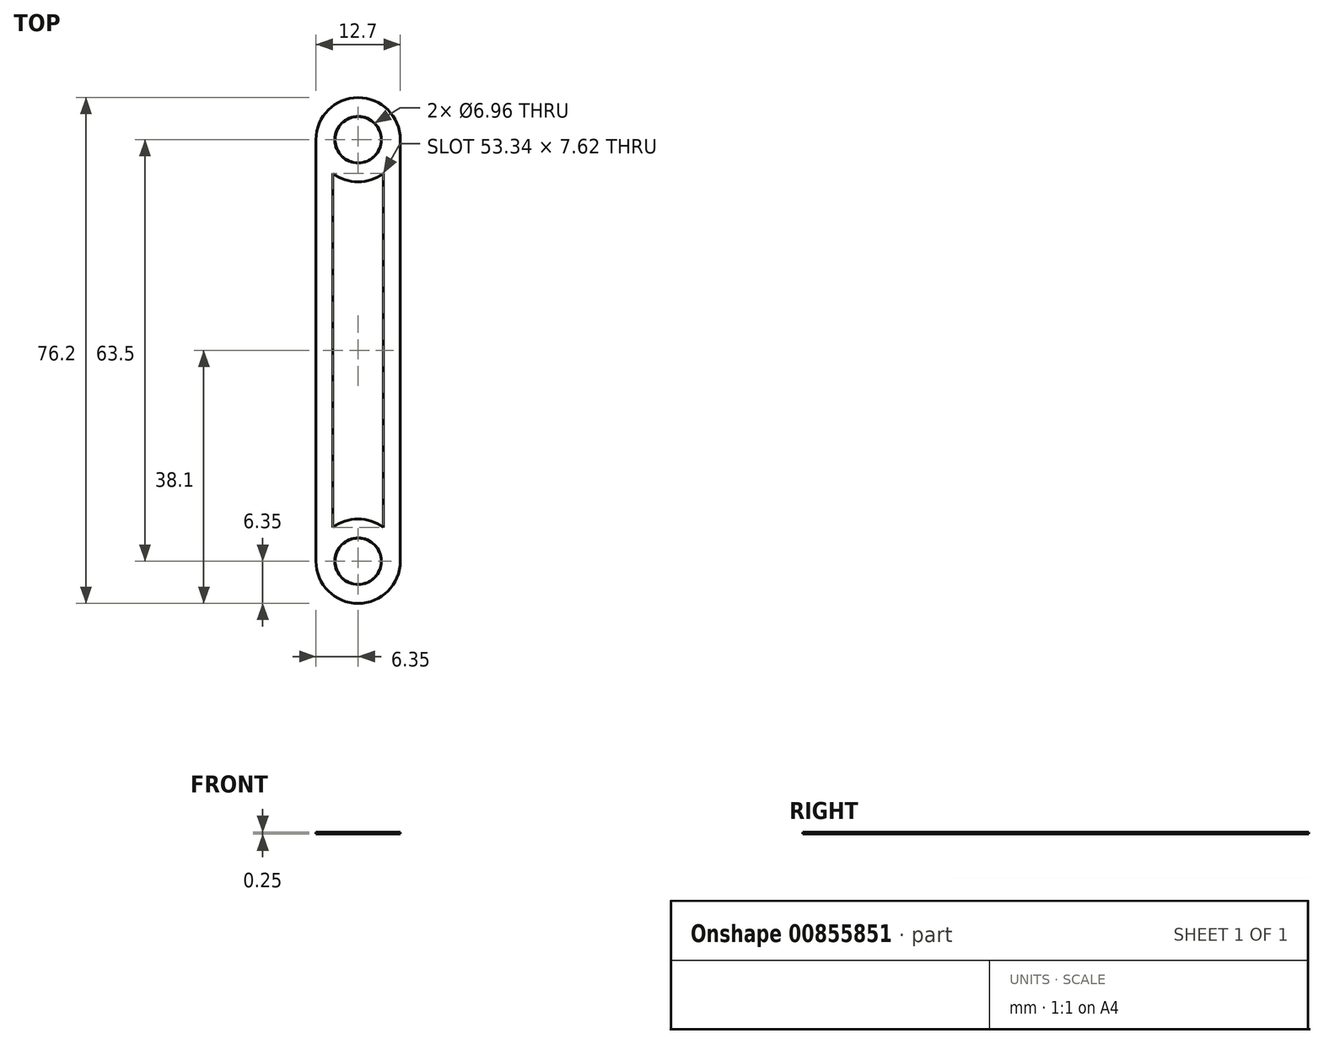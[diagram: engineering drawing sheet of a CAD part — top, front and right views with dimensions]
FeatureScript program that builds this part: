
annotation { "Feature Type Name" : "Feature", "Feature Type Description" : "" }
export const myFeature = defineFeature(function(context is Context, id is Id, definition is map)
    precondition{}
    {
        {
            assignVariable(context, id + "F0", {"name" : "ShaftDiameter", "anyValue" : 0.24});
        }
        {
            assignVariable(context, id + "F1", {"name" : "Thickness", "anyValue" : .25});
        }
        {
            var Q0;
            Q0=qCreatedBy(makeId("Top.planeOp"),FACE);
            var sketch = newSketch(context, id + "F2", { "sketchPlane" : qUnion([Q0])});
            skCircle(sketch, "E0", {"center": v(0, 0) * mm, "radius": 3.05 * mm, "construction": true});
            skCircle(sketch, "E1", {"center": v(0, 0) * mm, "radius": 6.35 * mm});
            skCircle(sketch, "E2", {"center": v(0, -63.5) * mm, "radius": 3.05 * mm, "construction": true});
            skCircle(sketch, "E3", {"center": v(0, -63.5) * mm, "radius": 6.35 * mm});
            skLineSegment(sketch, "E4", {"start": v(0, 41.86) * mm, "end": v(0, -87.11) * mm, "construction": true});
            skLineSegment(sketch, "E5", {"start": v(-6.35, 0) * mm, "end": v(-6.35, -63.5) * mm});
            skLineSegment(sketch, "E6", {"start": v(6.35, 0) * mm, "end": v(6.35, -63.5) * mm});
            skLineSegment(sketch, "E7", {"start": v(3.8, -5.08) * mm, "end": v(3.81, -58.42) * mm});
            skLineSegment(sketch, "E8.MirrorCS", {"start": v(-3.8, -5.08) * mm, "end": v(-3.81, -58.42) * mm});
            skCircle(sketch, "E9", {"center": v(0, 0) * mm, "radius": 3.48 * mm});
            skCircle(sketch, "E10", {"center": v(0, -63.5) * mm, "radius": 3.48 * mm});
            skSolve(sketch);
        }
        {
            var Q0;
            {var subQ0=sQuery(id+"F2.wireOp",EDGE,"E5");Q0=makeQuery(id+"F2.imprint","IMPRINT",FACE,{"disambiguationData":[TD([[makeQuery(id+"F2.imprint","IMPRINT",EDGE,{"derivedFrom":subQ0}),1.0]])]});}
            var Q1;
            Q1=makeQuery(id+"F2.imprint","IMPRINT",FACE,{"disambiguationData":[TD([[makeQuery(id+"F2.imprint","IMPRINT",EDGE,{"derivedFrom":sQuery(id+"F2.wireOp",EDGE,"E9")}),-1.0]])]});
            var Q2;
            {var subQ0=sQuery(id+"F2.wireOp",EDGE,"E6");Q2=makeQuery(id+"F2.imprint","IMPRINT",FACE,{"disambiguationData":[TD([[makeQuery(id+"F2.imprint","IMPRINT",EDGE,{"derivedFrom":subQ0}),-1.0]])]});}
            var Q3;
            Q3=makeQuery(id+"F2.imprint","IMPRINT",FACE,{"disambiguationData":[TD([[makeQuery(id+"F2.imprint","IMPRINT",EDGE,{"derivedFrom":sQuery(id+"F2.wireOp",EDGE,"E10")}),-1.0]])]});
            extrude(context, id + "F3", {"entities" : qUnion([Q0, Q1, Q2, Q3]), "depth" : (getVariable(context, 'Thickness')) * mm, "offsetDistance" : 25.4 * mm});
        }
        {
            var Q0;
            Q0=makeQuery(id+"F3.opExtrude","CAP_EDGE",EDGE,{"disambiguationData":[OSD([sQuery(id+"F2.wireOp",EDGE,"E9")])],"isStart":false});
            var Q1;
            Q1=makeQuery(id+"F3.opExtrude","CAP_EDGE",EDGE,{"disambiguationData":[OSD([sQuery(id+"F2.wireOp",EDGE,"E10")])],"isStart":false});
            var Q2;
            Q2=makeQuery(id+"F3.opExtrude","CAP_EDGE",EDGE,{"disambiguationData":[OSD([sQuery(id+"F2.wireOp",EDGE,"E9")])],"isStart":true});
            var Q3;
            Q3=makeQuery(id+"F3.opExtrude","CAP_EDGE",EDGE,{"disambiguationData":[OSD([sQuery(id+"F2.wireOp",EDGE,"E10")])],"isStart":true});
            chamfer(context, id + "F4", {"entities" : qUnion([Q0, Q1, Q2, Q3]), "chamferType" : ChamferType.OFFSET_ANGLE, "width" : (.1 * getVariable(context, 'ShaftDiameter')) * mm, "oppositeDirection" : false, "angle" : 45 * degree, "tangentPropagation" : true});
        }
    });
